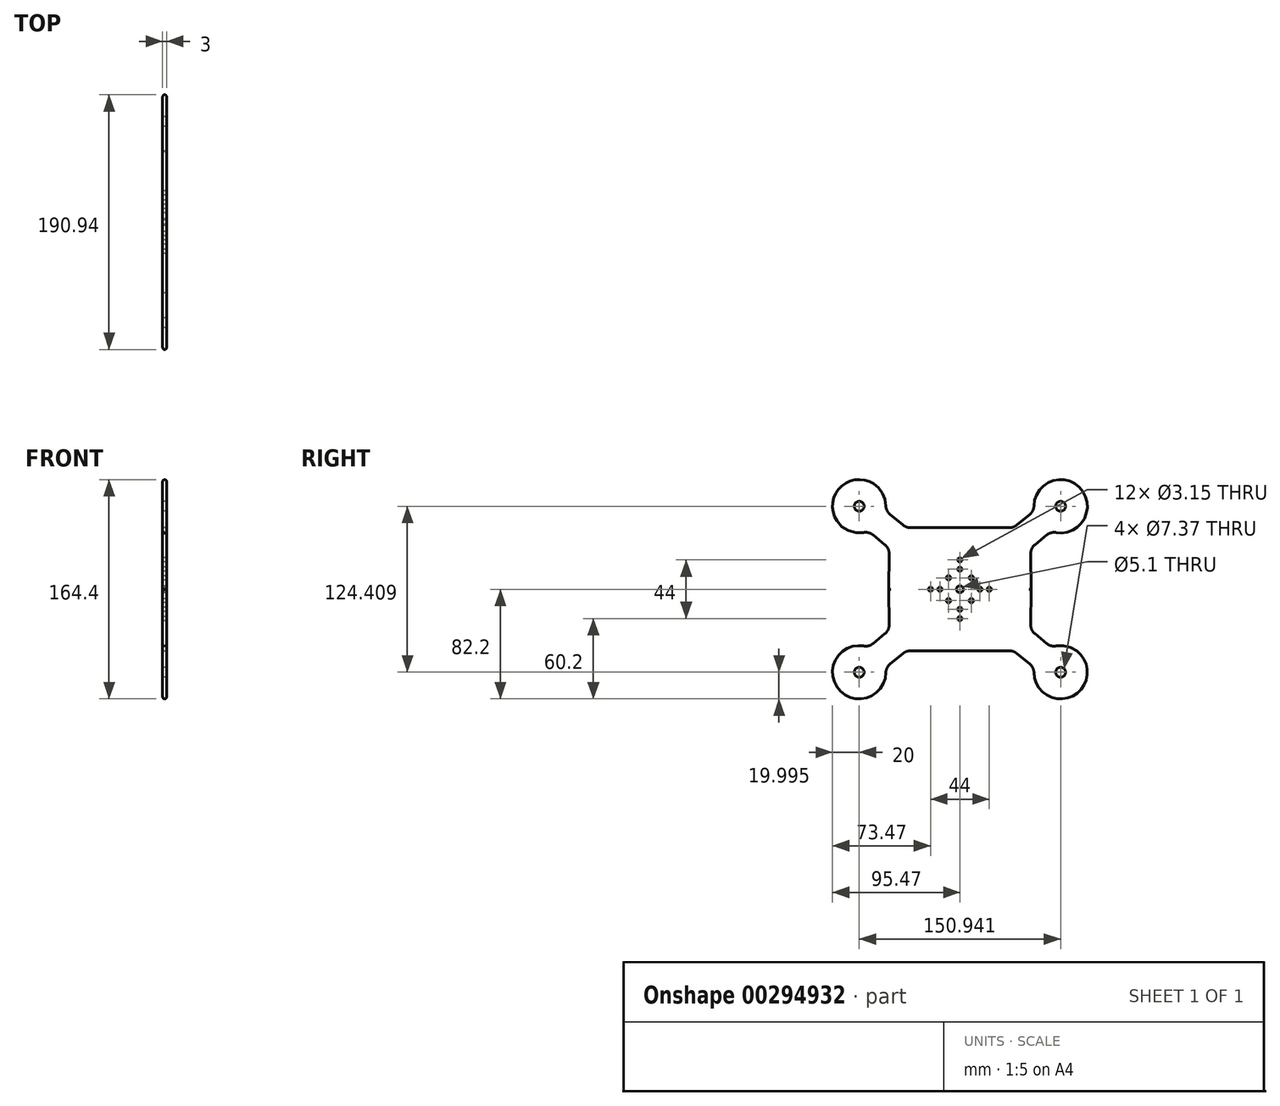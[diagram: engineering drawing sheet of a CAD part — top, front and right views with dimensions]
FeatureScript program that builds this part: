
annotation { "Feature Type Name" : "Feature", "Feature Type Description" : "" }
export const myFeature = defineFeature(function(context is Context, id is Id, definition is map)
    precondition{}
    {
        {
            var Q0;
            Q0=qCreatedBy(makeId("Right.planeOp"),FACE);
            var sketch = newSketch(context, id + "F0", { "sketchPlane" : qUnion([Q0])});
            skLineSegment(sketch, "E0.top", {"start": v(0, 46.18) * mm, "end": v(37.3, 46.18) * mm});
            skLineSegment(sketch, "E0.right", {"start": v(53.23, -4.94) * mm, "end": v(53.05, 26.77) * mm});
            skLineSegment(sketch, "E1", {"start": v(0, 0) * mm, "end": v(169.34, 139.57) * mm, "construction": true});
            skArc(sketch, "E2", {"start": v(71.95, 42.52) * mm, "mid": v(90.9, 74.93) * mm, "end": v(55.47, 62.5) * mm});
            skLineSegment(sketch, "E3", {"start": v(42.63, 48.1) * mm, "end": v(52.42, 56.17) * mm});
            skLineSegment(sketch, "E4.MirrorCS", {"start": v(56.1, 33.28) * mm, "end": v(65.14, 40.73) * mm});
            skCircle(sketch, "E5", {"center": v(75.47, 62.2) * mm, "radius": 3.68 * mm});
            skPoint(sketch, "E6.visualSharp", {"position": v(40.31, 46.18) * mm});
            skArc(sketch, "E6.filletArc", {"start": v(37.3, 46.18) * mm, "mid": v(40.13, 46.68) * mm, "end": v(42.63, 48.1) * mm});
            skPoint(sketch, "E7.visualSharp", {"position": v(53.03, 30.75) * mm});
            skArc(sketch, "E7.filletArc", {"start": v(56.1, 33.28) * mm, "mid": v(53.84, 30.37) * mm, "end": v(53.05, 26.77) * mm});
            skPoint(sketch, "E8.visualSharp", {"position": v(68.46, 43.47) * mm});
            skArc(sketch, "E8.filletArc", {"start": v(71.95, 42.52) * mm, "mid": v(68.35, 42.37) * mm, "end": v(65.14, 40.73) * mm});
            skPoint(sketch, "E9.visualSharp", {"position": v(55.74, 58.9) * mm});
            skArc(sketch, "E9.filletArc", {"start": v(52.42, 56.17) * mm, "mid": v(54.65, 59) * mm, "end": v(55.47, 62.5) * mm});
            skArc(sketch, "E10.MirrorCS", {"start": v(-52.42, 56.17) * mm, "mid": v(-54.65, 59) * mm, "end": v(-55.47, 62.5) * mm});
            skArc(sketch, "E11.MirrorCS", {"start": v(-56.1, 33.28) * mm, "mid": v(-53.84, 30.37) * mm, "end": v(-53.05, 26.77) * mm});
            skArc(sketch, "E12.MirrorCS", {"start": v(-37.3, 46.18) * mm, "mid": v(-40.13, 46.68) * mm, "end": v(-42.63, 48.1) * mm});
            skArc(sketch, "E13.MirrorCS", {"start": v(-71.95, 42.52) * mm, "mid": v(-68.35, 42.37) * mm, "end": v(-65.14, 40.73) * mm});
            skPoint(sketch, "E14.MirrorP", {"position": v(-40.31, 46.18) * mm});
            skPoint(sketch, "E15.MirrorP", {"position": v(-53.03, 30.75) * mm});
            skPoint(sketch, "E16.MirrorP", {"position": v(-68.46, 43.47) * mm});
            skCircle(sketch, "E17.MirrorC", {"center": v(-75.47, 62.2) * mm, "radius": 3.68 * mm});
            skLineSegment(sketch, "E18.MirrorCS", {"start": v(-56.1, 33.28) * mm, "end": v(-65.14, 40.73) * mm});
            skLineSegment(sketch, "E19.MirrorCS", {"start": v(-42.63, 48.1) * mm, "end": v(-52.42, 56.17) * mm});
            skPoint(sketch, "E20.MirrorP", {"position": v(-55.74, 58.9) * mm});
            skArc(sketch, "E21.MirrorCS", {"start": v(-71.95, 42.52) * mm, "mid": v(-90.9, 74.93) * mm, "end": v(-55.47, 62.5) * mm});
            skLineSegment(sketch, "E22.MirrorCS", {"start": v(-53.23, -4.94) * mm, "end": v(-53.05, 26.77) * mm});
            skLineSegment(sketch, "E23.MirrorCS", {"start": v(0, 46.18) * mm, "end": v(-37.3, 46.18) * mm});
            skArc(sketch, "E24.MirrorCS", {"start": v(-56.1, -33.28) * mm, "mid": v(-53.84, -30.37) * mm, "end": v(-53.05, -26.77) * mm});
            skArc(sketch, "E25.MirrorCS", {"start": v(-37.3, -46.18) * mm, "mid": v(-40.13, -46.68) * mm, "end": v(-42.63, -48.1) * mm});
            skArc(sketch, "E26.MirrorCS", {"start": v(52.42, -56.17) * mm, "mid": v(54.65, -59) * mm, "end": v(55.47, -62.5) * mm});
            skArc(sketch, "E27.MirrorCS", {"start": v(71.95, -42.52) * mm, "mid": v(68.35, -42.37) * mm, "end": v(65.14, -40.73) * mm});
            skArc(sketch, "E28.MirrorCS", {"start": v(56.1, -33.28) * mm, "mid": v(53.84, -30.37) * mm, "end": v(53.05, -26.77) * mm});
            skArc(sketch, "E29.MirrorCS", {"start": v(37.3, -46.18) * mm, "mid": v(40.13, -46.68) * mm, "end": v(42.63, -48.1) * mm});
            skLineSegment(sketch, "E30.MirrorCS", {"start": v(56.1, -33.28) * mm, "end": v(65.14, -40.73) * mm});
            skLineSegment(sketch, "E31.MirrorCS", {"start": v(42.63, -48.1) * mm, "end": v(52.42, -56.17) * mm});
            skArc(sketch, "E32.MirrorCS", {"start": v(-71.95, -42.52) * mm, "mid": v(-68.35, -42.37) * mm, "end": v(-65.14, -40.73) * mm});
            skLineSegment(sketch, "E33.MirrorCS", {"start": v(-42.63, -48.1) * mm, "end": v(-52.42, -56.17) * mm});
            skCircle(sketch, "E34.MirrorC", {"center": v(-75.47, -62.2) * mm, "radius": 3.68 * mm});
            skArc(sketch, "E35.MirrorCS", {"start": v(-52.42, -56.17) * mm, "mid": v(-54.65, -59) * mm, "end": v(-55.47, -62.5) * mm});
            skLineSegment(sketch, "E36.MirrorCS", {"start": v(-56.1, -33.28) * mm, "end": v(-65.14, -40.73) * mm});
            skCircle(sketch, "E37.MirrorC", {"center": v(75.47, -62.2) * mm, "radius": 3.68 * mm});
            skPoint(sketch, "E38.MirrorP", {"position": v(53.03, -30.75) * mm});
            skPoint(sketch, "E39.MirrorP", {"position": v(40.31, -46.18) * mm});
            skPoint(sketch, "E40.MirrorP", {"position": v(-55.74, -58.9) * mm});
            skPoint(sketch, "E41.MirrorP", {"position": v(-68.46, -43.47) * mm});
            skPoint(sketch, "E42.MirrorP", {"position": v(-40.31, -46.18) * mm});
            skArc(sketch, "E43.MirrorCS", {"start": v(71.95, -42.52) * mm, "mid": v(90.9, -74.93) * mm, "end": v(55.47, -62.5) * mm});
            skArc(sketch, "E44.MirrorCS", {"start": v(-71.95, -42.52) * mm, "mid": v(-90.9, -74.93) * mm, "end": v(-55.47, -62.5) * mm});
            skPoint(sketch, "E45.MirrorP", {"position": v(68.46, -43.47) * mm});
            skPoint(sketch, "E46.MirrorP", {"position": v(55.74, -58.9) * mm});
            skLineSegment(sketch, "E47.MirrorCS", {"start": v(0, -46.18) * mm, "end": v(-37.3, -46.18) * mm});
            skLineSegment(sketch, "E48.MirrorCS", {"start": v(0, -46.18) * mm, "end": v(37.3, -46.18) * mm});
            skPoint(sketch, "E49.MirrorP", {"position": v(-53.03, -30.75) * mm});
            skLineSegment(sketch, "E50.MirrorCS", {"start": v(-53.23, 4.94) * mm, "end": v(-53.05, -26.77) * mm});
            skLineSegment(sketch, "E51.MirrorCS", {"start": v(53.23, 4.94) * mm, "end": v(53.05, -26.77) * mm});
            skCircle(sketch, "E52", {"center": v(0, 0) * mm, "radius": 2.55 * mm});
            skCircle(sketch, "E53", {"center": v(0, 15) * mm, "radius": 1.57 * mm});
            skCircle(sketch, "E54", {"center": v(0, 22) * mm, "radius": 1.57 * mm});
            skCircle(sketch, "E55", {"center": v(15, 0) * mm, "radius": 1.57 * mm});
            skCircle(sketch, "E56", {"center": v(22, 0) * mm, "radius": 1.57 * mm});
            skCircle(sketch, "E57", {"center": v(-8.55, 8.55) * mm, "radius": 1.57 * mm});
            skCircle(sketch, "E58.MirrorC", {"center": v(0, -15) * mm, "radius": 1.57 * mm});
            skCircle(sketch, "E59.MirrorC", {"center": v(0, -22) * mm, "radius": 1.57 * mm});
            skCircle(sketch, "E60.MirrorC", {"center": v(-8.55, -8.55) * mm, "radius": 1.57 * mm});
            skCircle(sketch, "E61.MirrorC", {"center": v(-15, 0) * mm, "radius": 1.57 * mm});
            skCircle(sketch, "E62.MirrorC", {"center": v(-22, 0) * mm, "radius": 1.57 * mm});
            skCircle(sketch, "E63.MirrorC", {"center": v(8.55, 8.55) * mm, "radius": 1.57 * mm});
            skCircle(sketch, "E64.MirrorC", {"center": v(8.55, -8.55) * mm, "radius": 1.57 * mm});
            skSolve(sketch);
        }
        {
            var Q0;
            Q0=makeQuery(id+"F0.imprint","IMPRINT",FACE,{"disambiguationData":[TD([[makeQuery(id+"F0.imprint","IMPRINT",EDGE,{"derivedFrom":sQuery(id+"F0.wireOp",EDGE,"E0.top")}),-1.0]])]});
            extrude(context, id + "F1", {"entities" : qUnion([Q0]), "depth" : 3 * mm});
        }
        {
            var Q0;
            Q0=makeQuery(id+"F1.opExtrude","CAP_EDGE",EDGE,{"disambiguationData":[OSD([sQuery(id+"F0.wireOp",EDGE,"E0.top"),sQuery(id+"F0.wireOp",EDGE,"E23.MirrorCS")])],"isStart":true});
            var Q1;
            Q1=makeQuery(id+"F1.opExtrude","CAP_EDGE",EDGE,{"disambiguationData":[OSD([sQuery(id+"F0.wireOp",EDGE,"E6.filletArc")])],"isStart":true});
            var Q2;
            Q2=makeQuery(id+"F1.opExtrude","CAP_EDGE",EDGE,{"disambiguationData":[OSD([sQuery(id+"F0.wireOp",EDGE,"E3")])],"isStart":true});
            var Q3;
            Q3=makeQuery(id+"F1.opExtrude","CAP_EDGE",EDGE,{"disambiguationData":[OSD([sQuery(id+"F0.wireOp",EDGE,"E9.filletArc")])],"isStart":true});
            var Q4;
            Q4=makeQuery(id+"F1.opExtrude","CAP_EDGE",EDGE,{"disambiguationData":[OSD([sQuery(id+"F0.wireOp",EDGE,"E2")])],"isStart":true});
            var Q5;
            Q5=makeQuery(id+"F1.opExtrude","CAP_EDGE",EDGE,{"disambiguationData":[OSD([sQuery(id+"F0.wireOp",EDGE,"E8.filletArc")])],"isStart":true});
            var Q6;
            Q6=makeQuery(id+"F1.opExtrude","CAP_EDGE",EDGE,{"disambiguationData":[OSD([sQuery(id+"F0.wireOp",EDGE,"E4.MirrorCS")])],"isStart":true});
            var Q7;
            Q7=makeQuery(id+"F1.opExtrude","CAP_EDGE",EDGE,{"disambiguationData":[OSD([sQuery(id+"F0.wireOp",EDGE,"E7.filletArc")])],"isStart":true});
            var Q8;
            Q8=makeQuery(id+"F1.opExtrude","CAP_EDGE",EDGE,{"disambiguationData":[OSD([sQuery(id+"F0.wireOp",EDGE,"E0.right")])],"isStart":true});
            var Q9;
            Q9=makeQuery(id+"F1.opExtrude","CAP_EDGE",EDGE,{"disambiguationData":[OSD([sQuery(id+"F0.wireOp",EDGE,"E51.MirrorCS")])],"isStart":true});
            var Q10;
            Q10=makeQuery(id+"F1.opExtrude","CAP_EDGE",EDGE,{"disambiguationData":[OSD([sQuery(id+"F0.wireOp",EDGE,"E28.MirrorCS")])],"isStart":true});
            var Q11;
            Q11=makeQuery(id+"F1.opExtrude","CAP_EDGE",EDGE,{"disambiguationData":[OSD([sQuery(id+"F0.wireOp",EDGE,"E0.top"),sQuery(id+"F0.wireOp",EDGE,"E23.MirrorCS")])],"isStart":false});
            var Q12;
            Q12=makeQuery(id+"F1.opExtrude","CAP_EDGE",EDGE,{"disambiguationData":[OSD([sQuery(id+"F0.wireOp",EDGE,"E12.MirrorCS")])],"isStart":false});
            var Q13;
            Q13=makeQuery(id+"F1.opExtrude","CAP_EDGE",EDGE,{"disambiguationData":[OSD([sQuery(id+"F0.wireOp",EDGE,"E19.MirrorCS")])],"isStart":false});
            var Q14;
            Q14=makeQuery(id+"F1.opExtrude","CAP_EDGE",EDGE,{"disambiguationData":[OSD([sQuery(id+"F0.wireOp",EDGE,"E10.MirrorCS")])],"isStart":false});
            var Q15;
            Q15=makeQuery(id+"F1.opExtrude","CAP_EDGE",EDGE,{"disambiguationData":[OSD([sQuery(id+"F0.wireOp",EDGE,"E21.MirrorCS")])],"isStart":false});
            var Q16;
            Q16=makeQuery(id+"F1.opExtrude","CAP_EDGE",EDGE,{"disambiguationData":[OSD([sQuery(id+"F0.wireOp",EDGE,"E13.MirrorCS")])],"isStart":false});
            var Q17;
            Q17=makeQuery(id+"F1.opExtrude","CAP_EDGE",EDGE,{"disambiguationData":[OSD([sQuery(id+"F0.wireOp",EDGE,"E18.MirrorCS")])],"isStart":false});
            var Q18;
            Q18=makeQuery(id+"F1.opExtrude","CAP_EDGE",EDGE,{"disambiguationData":[OSD([sQuery(id+"F0.wireOp",EDGE,"E11.MirrorCS")])],"isStart":false});
            var Q19;
            Q19=makeQuery(id+"F1.opExtrude","CAP_EDGE",EDGE,{"disambiguationData":[OSD([sQuery(id+"F0.wireOp",EDGE,"E22.MirrorCS")])],"isStart":false});
            var Q20;
            Q20=makeQuery(id+"F1.opExtrude","CAP_EDGE",EDGE,{"disambiguationData":[OSD([sQuery(id+"F0.wireOp",EDGE,"E50.MirrorCS")])],"isStart":false});
            fillet(context, id + "F2", {"entities" : qUnion([Q0, Q1, Q2, Q3, Q4, Q5, Q6, Q7, Q8, Q9, Q10, Q11, Q12, Q13, Q14, Q15, Q16, Q17, Q18, Q19, Q20]), "radius" : 1.5 * mm, "tangentPropagation" : true, "allowEdgeOverflow" : false});
        }
    });
